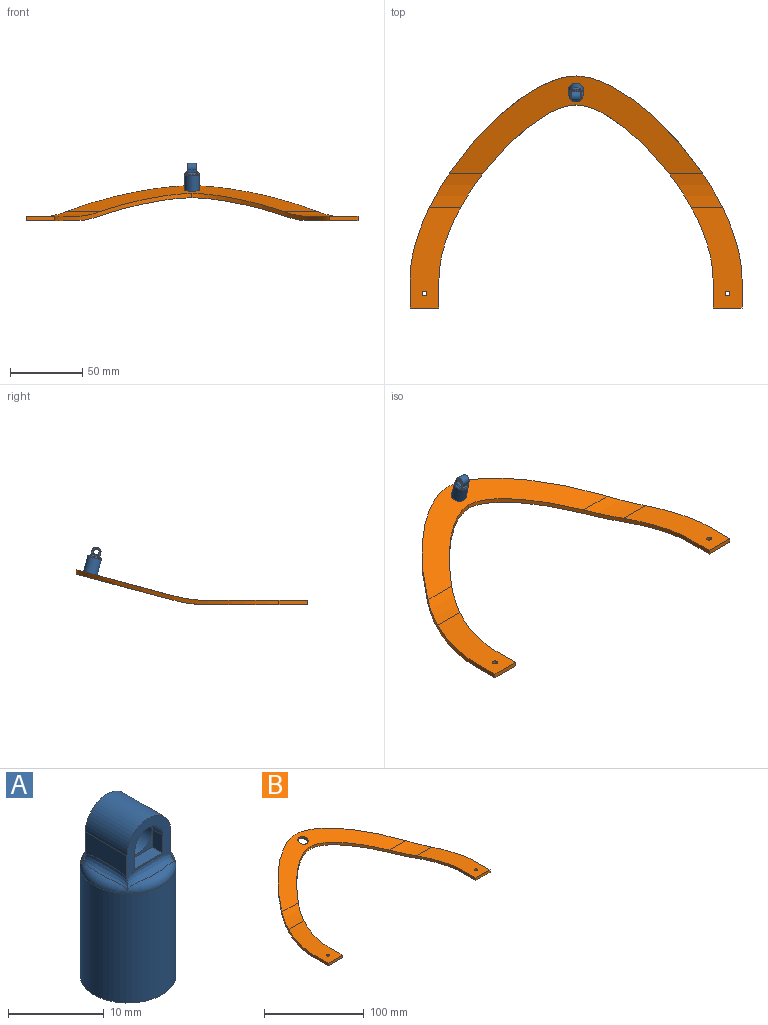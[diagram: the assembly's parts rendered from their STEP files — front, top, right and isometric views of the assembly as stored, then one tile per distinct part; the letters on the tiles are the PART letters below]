
ASSEMBLY  parts=2 mates=1
PART A: 23 faces, bbox 10.8x10.8x21.7 mm
  f0: plane 2.28x1.5mm, normal (-1,0,0), area 3.4mm2, adj f1,f3,f12,f15
  f1: plane 4.15x1.5mm, normal (0,0,1), area 6.2mm2, adj f0,f2,f12,f15
  f2: plane 2.28x1.5mm, normal (1,0,0), area 3.4mm2, adj f1,f3,f12,f15
  f3: cylinder r=2.08mm len=4.15mm, axis (0,1,0), area 9.8mm2, adj f0,f2,f12,f15
  f4: plane 6.15x2.85mm, normal (-1,0,0), area 15.6mm2, adj f10,f11,f12,f19,f21,f22
  f5: plane 6.15x2.85mm, normal (1,0,0), area 15.6mm2, adj f10,f11,f12,f19,f20,f22
  f6: cylinder r=2.08mm len=4.15mm, axis (0,1,0), area 9.8mm2, adj f7,f9,f11,f14
  f7: plane 2.28x1.5mm, normal (-1,0,0), area 3.4mm2, adj f6,f8,f11,f14
  f8: plane 4.15x1.5mm, normal (0,0,1), area 6.2mm2, adj f7,f9,f11,f14
  f9: plane 2.28x1.5mm, normal (1,0,0), area 3.4mm2, adj f6,f8,f11,f14
  f10: cylinder r=3.23mm len=6.45mm, axis (0,1,0), area 62.3mm2, adj f4,f5,f11,f12
  f11: plane 6.45x6.05mm, normal (0,-1,0), area 16.3mm2, adj f4,f5,f6,f7,f8,f9,f10,f22
  f12: plane 6.45x6.05mm, normal (0,1,0), area 16.3mm2, adj f0,f1,f2,f3,f4,f5,f10,f19
  f13: cylinder r=1.95mm len=3.9mm, axis (0,1,0), area 38.6mm2, adj f14,f15
  f14: plane 4.35x4.15mm, normal (0,-1,0), area 4.3mm2, adj f6,f7,f8,f9,f13
  f15: plane 4.35x4.15mm, normal (0,1,0), area 4.3mm2, adj f0,f1,f2,f3,f13
  f16: cylinder r=5mm len=14mm, axis (0,0,1), area 439.8mm2, adj f17,f18
  f17: plane 10x10mm, normal (0,0,-1), area 78.5mm2, adj f16
  f18: torus R=4mm, axis (0,0,-1), area 35.1mm2, adj f16,f19,f20,f21,f22
  f19: bspline ~8.68x1.79mm, area 9.1mm2, adj f4,f5,f12,f18,f20,f21
  f20: bspline ~8.37x1.8mm, area 8.6mm2, adj f5,f18,f19,f22
  f21: bspline ~8.37x1.8mm, area 8.6mm2, adj f4,f18,f19,f22
  f22: bspline ~8.68x1.78mm, area 9.1mm2, adj f4,f5,f11,f18,f20,f21
PART B: 23 faces, bbox 229x160x24.2 mm
  f0: plane 175.08x67.56mm, normal (0,-0.26,0.97), area 3767.3mm2, adj f2,f3,f4,f5,f18,f19,f22
  f1: plane 175.08x67.57mm, normal (0,0.26,-0.97), area 3767.2mm2, adj f2,f3,f4,f5,f20,f21,f22
  f2: extruded ~120x94.5mm, area 485.5mm2, adj f0,f1,f5,f6,f7,f10,f18,f20
  f3: extruded ~140x114.5mm, area 576.7mm2, adj f0,f1,f4,f6,f7,f8,f18,f20
  f4: extruded ~140x114.5mm, area 576.7mm2, adj f0,f1,f3,f14,f15,f16,f19,f21
  f5: extruded ~120x94.5mm, area 485.5mm2, adj f0,f1,f2,f12,f15,f16,f19,f21
  f6: plane 69.85x35.58mm, normal (0,0,1), area 1400.7mm2, adj f2,f3,f8,f9,f10,f11,f18
  f7: plane 69.85x35.58mm, normal (0,0,-1), area 1400.7mm2, adj f2,f3,f8,f9,f10,f11,f20
  f8: plane 20x3mm, normal (-1,0,0), area 60mm2, adj f3,f6,f7,f9
  f9: plane 20x3mm, normal (0,-1,0), area 60mm2, adj f6,f7,f8,f10
  f10: plane 20x3mm, normal (1,0,0), area 60mm2, adj f2,f6,f7,f9
  f11: cylinder r=1.7mm len=3.4mm, axis (0,0,-1), area 32mm2, adj f6,f7
  f12: plane 20x3mm, normal (-1,0,0), area 60mm2, adj f5,f13,f15,f16
  f13: plane 20x3mm, normal (0,-1,0), area 60mm2, adj f12,f14,f15,f16
  f14: plane 20x3mm, normal (1,0,0), area 60mm2, adj f4,f13,f15,f16
  f15: plane 69.85x35.58mm, normal (0,0,1), area 1400.7mm2, adj f4,f5,f12,f13,f14,f17,f19
  f16: plane 69.85x35.58mm, normal (0,0,-1), area 1400.7mm2, adj f4,f5,f12,f13,f14,f17,f21
  f17: cylinder r=1.7mm len=3.4mm, axis (0,0,-1), area 32mm2, adj f15,f16
  f18: cylinder r=90mm len=36.75mm, axis (-1,0,0), area 524.8mm2, adj f0,f2,f3,f6
  f19: cylinder r=90mm len=36.75mm, axis (-1,0,0), area 524.8mm2, adj f0,f4,f5,f15
  f20: cylinder r=90mm len=36.75mm, axis (-1,0,0), area 524.8mm2, adj f1,f2,f3,f7
  f21: cylinder r=90mm len=36.75mm, axis (-1,0,0), area 524.8mm2, adj f1,f4,f5,f16
  f22: cylinder r=5.25mm len=10.89mm, axis (0,-0.26,0.97), area 95.6mm2, adj f0,f1
PLACE A rot(axis=(0.13,0.13,-0.98),91deg) t=(-14.67,48.79,31.6)mm
PLACE B t=(-14.67,61.92,-1.58)mm
MATE revolute A.f16 <-> B.f22  axis (0,-0.26,0.97) through (-14.67,52.67,17.11)mm
